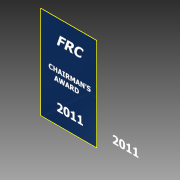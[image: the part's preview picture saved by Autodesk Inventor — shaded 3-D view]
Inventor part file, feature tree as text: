
AUTODESK INVENTOR PART (.ipt)
format: ipt  version: 2014 (Build 180170000, 170)  size: 86,016 bytes
history: native  units: in
note: dims shown in document units (in); Inventor stores cm internally (conversion verified against a paired STEP export)
features: sketch x3, extrude x1
ambient origin geometry x8: Origin, YZ Plane, XZ Plane, XY Plane, X Axis, Y Axis, Z Axis, Center Point
bodies: Solid1 (feature_tree)
feature tree (4):
  extrude  "Extrusion1"  Depth=60.0in
  sketch  "Sketch2"  dims[d2=0.2in d3=0.0in]
  sketch  "Sketch3"
  sketch  "Sketch1"  dims[d0=36.0in d1=60.0in]
